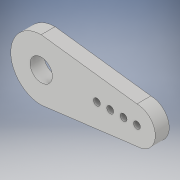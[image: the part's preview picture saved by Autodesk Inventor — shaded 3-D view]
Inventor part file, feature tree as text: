
AUTODESK INVENTOR PART (.ipt)
format: ipt  version: 2019 (Build 230136000, 136)  size: 118,272 bytes
history: native  units: in
note: dims shown in document units (in); Inventor stores cm internally (conversion verified against a paired STEP export)
features: extrude x2, sketch x2
ambient origin geometry x8: Origin, YZ Plane, XZ Plane, XY Plane, X Axis, Y Axis, Z Axis, Center Point
bodies: Solid1 (feature_tree)
feature tree (4):
  extrude  "Extrusion1"  Depth=0.33in
  extrude  "Extrusion2"  Depth=0.125in TaperAngle=0.0deg
  sketch  "Sketch1"  dims[d0=0.547in d1=0.33in]
  sketch  "Sketch2"  dims[d2=0.86in d3=0.125in d4=0.0in d5=0.2in d6=0.062in d7=0.062in d8=0.062in d9=0.062in d10=0.5in d11=0.62in d12=0.74in d13=0.86in d14=0.125in d15=0.0in]
